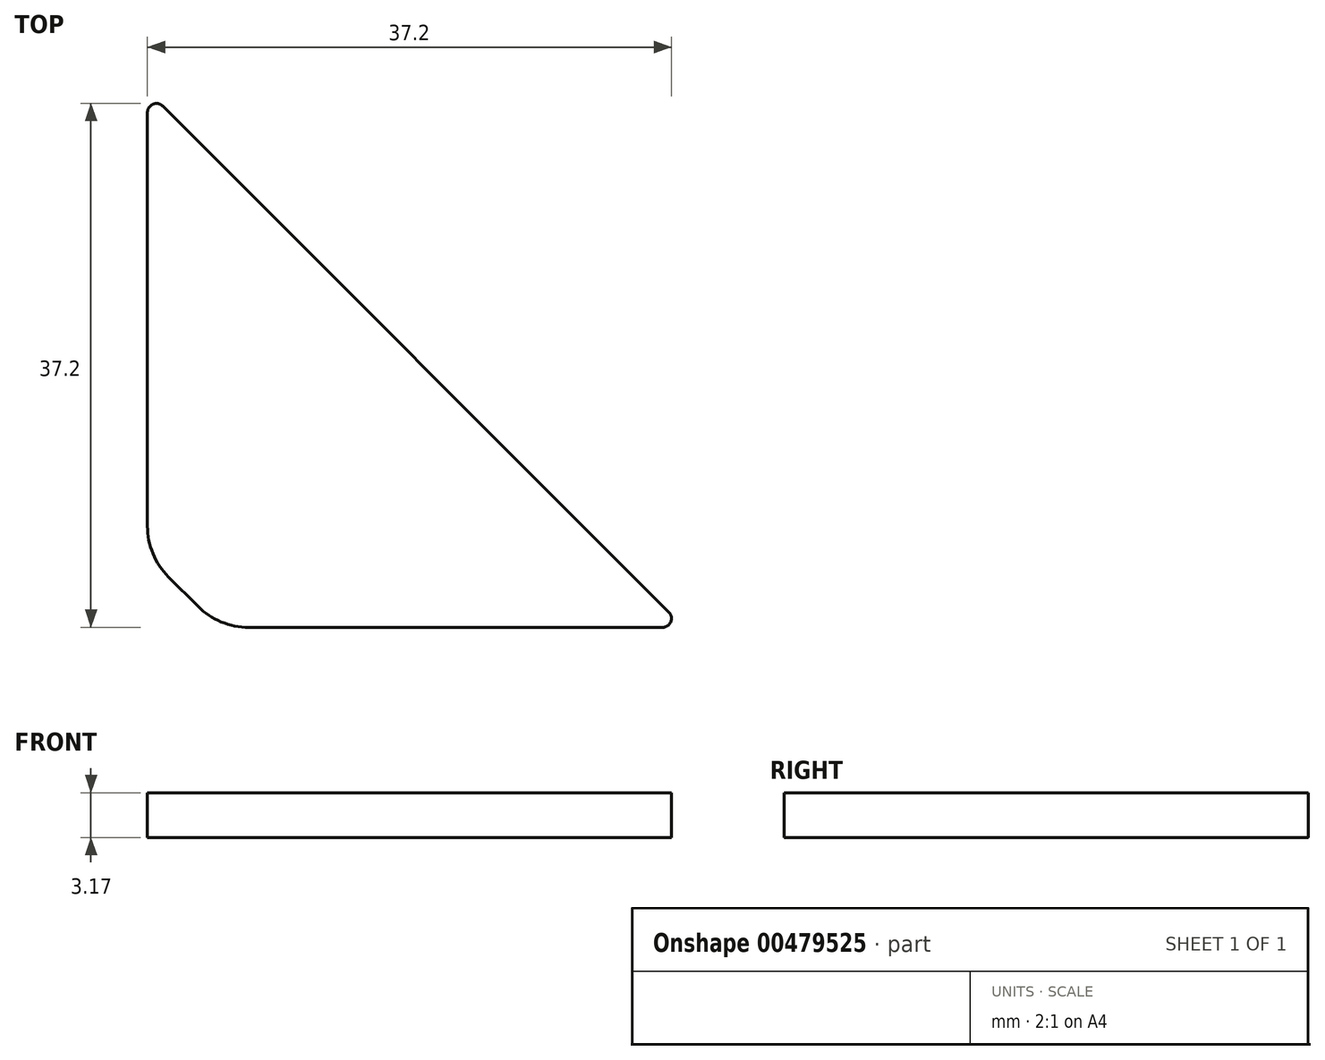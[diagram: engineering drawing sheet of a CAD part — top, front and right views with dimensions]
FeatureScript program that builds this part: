
annotation { "Feature Type Name" : "Feature", "Feature Type Description" : "" }
export const myFeature = defineFeature(function(context is Context, id is Id, definition is map)
    precondition{}
    {
        {
            var Q0;
            Q0=qCreatedBy(makeId("Top.planeOp"),FACE);
            var sketch = newSketch(context, id + "F0", { "sketchPlane" : qUnion([Q0])});
            skLineSegment(sketch, "E0", {"start": v(5.08, 0) * mm, "end": v(38.1, 0) * mm});
            skLineSegment(sketch, "E1", {"start": v(38.1, 0) * mm, "end": v(0, 38.1) * mm});
            skLineSegment(sketch, "E2", {"start": v(0, 5.08) * mm, "end": v(0, 38.1) * mm});
            skPoint(sketch, "E3", {"position": v(0, 5.08) * mm});
            skPoint(sketch, "E4", {"position": v(5.08, 0) * mm});
            skLineSegment(sketch, "E5", {"start": v(0, 5.08) * mm, "end": v(5.08, 0) * mm});
            skPoint(sketch, "E6.orphan", {"position": v(0, 0) * mm});
            skSolve(sketch);
        }
        {
            var Q0;
            Q0=makeQuery(id+"F0.imprint","IMPRINT",FACE,{"disambiguationData":[TD([[makeQuery(id+"F0.imprint","IMPRINT",EDGE,{"derivedFrom":sQuery(id+"F0.wireOp",EDGE,"E0")}),1.0]])]});
            extrude(context, id + "F1", {"entities" : qUnion([Q0]), "depth" : 3.17 * mm});
        }
        {
            var Q0;
            Q0=makeQuery(id+"F1.opExtrude","SWEPT_EDGE",EDGE,{"disambiguationData":[OSD([sQuery(id+"F0.wireOp",EDGE,"E1"),sQuery(id+"F0.wireOp",EDGE,"E2")])]});
            var Q1;
            Q1=makeQuery(id+"F1.opExtrude","SWEPT_EDGE",EDGE,{"disambiguationData":[OSD([sQuery(id+"F0.wireOp",EDGE,"E0"),sQuery(id+"F0.wireOp",EDGE,"E1")])]});
            fillet(context, id + "F2", {"entities" : qUnion([Q0, Q1]), "radius" : 0.64 * mm, "tangentPropagation" : true, "allowEdgeOverflow" : false});
        }
        {
            var Q0;
            Q0=makeQuery(id+"F1.opExtrude","SWEPT_EDGE",EDGE,{"disambiguationData":[OSD([sQuery(id+"F0.wireOp",EDGE,"E0"),sQuery(id+"F0.wireOp",EDGE,"E5")])]});
            var Q1;
            Q1=makeQuery(id+"F1.opExtrude","SWEPT_EDGE",EDGE,{"disambiguationData":[OSD([sQuery(id+"F0.wireOp",EDGE,"E2"),sQuery(id+"F0.wireOp",EDGE,"E5")])]});
            fillet(context, id + "F3", {"entities" : qUnion([Q0, Q1]), "radius" : 5.08 * mm, "tangentPropagation" : true, "allowEdgeOverflow" : false});
        }
    });
